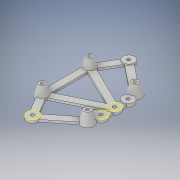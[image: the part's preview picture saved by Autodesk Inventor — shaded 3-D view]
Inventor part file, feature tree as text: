
AUTODESK INVENTOR PART (.ipt)
format: ipt  version: 2019 (Build 230136000, 136)  size: 312,320 bytes
history: native  units: mm
features: sketch x9, extrude x4, projected_geometry x3, hole x2, draft x1
ambient origin geometry x8: Origin, YZ Plane, XZ Plane, XY Plane, X Axis, Y Axis, Z Axis, Center Point
bodies: Solid1 (feature_tree)
feature tree (19):
  sketch  "Sketch1"  dims[d0=85.0mm d1=12.0mm]
  extrude  "Extrusion1"  Depth=12.0mm
  hole  "Hole1"  [1 undecoded]
  sketch  "Sketch Driven Pattern1"  dims[d2=12.0mm d3=30.0mm]
  sketch  "Sketch4"  dims[d9=3.0mm d10=6.0mm d11=10.0mm d12=2.0mm d13=90.0deg d14=8.0mm d15=0.0mm d16=40.0mm]
  extrude  "Extrusion2"  Depth=30.5mm
  hole  "Hole2"  [1 undecoded]
  extrude  "Extrusion3"  Depth=10.0mm
  extrude  "Extrusion4"  Depth=3.0mm
  draft  "FaceDraft1"
  sketch  "Sketch2"  dims[d4=30.5mm d5=30.5mm]
  sketch  "Sketch3"  dims[d6=10.0mm d7=3.0mm d8=0.0mm]
  projected_geometry  "Projected Loop1"
  sketch  "Sketch5"  dims[d17=42.0mm d18=3.0mm]
  sketch  "Sketch7"  dims[d19=21.5mm]
  sketch  "Sketch8"  dims[d20=21.5mm]
  sketch  "Sketch9"  dims[d21=10.0mm d22=10.0mm d23=10.0mm d24=10.0mm d25=10.0mm d26=0.0mm d27=3.0mm d28=6.0mm d29=10.0mm d30=2.0mm d31=90.0deg d32=8.0mm d33=0.0mm d34=6.0mm d35=6.0mm d36=6.0mm d37=6.0mm d38=6.0mm d39=6.0mm d40=2.0mm d41=0.0mm d42=6.0mm d43=6.0mm d44=2.0mm d45=0.0mm d46=15.0deg]
  projected_geometry  "Project Cut Edges1"
  projected_geometry  "Project Cut Edges2"
note: 2 required parameter values undecoded (feature->parameter linkage not recoverable at this tier; creation-order binding heuristic only, values carry confidence <= 0.55)
